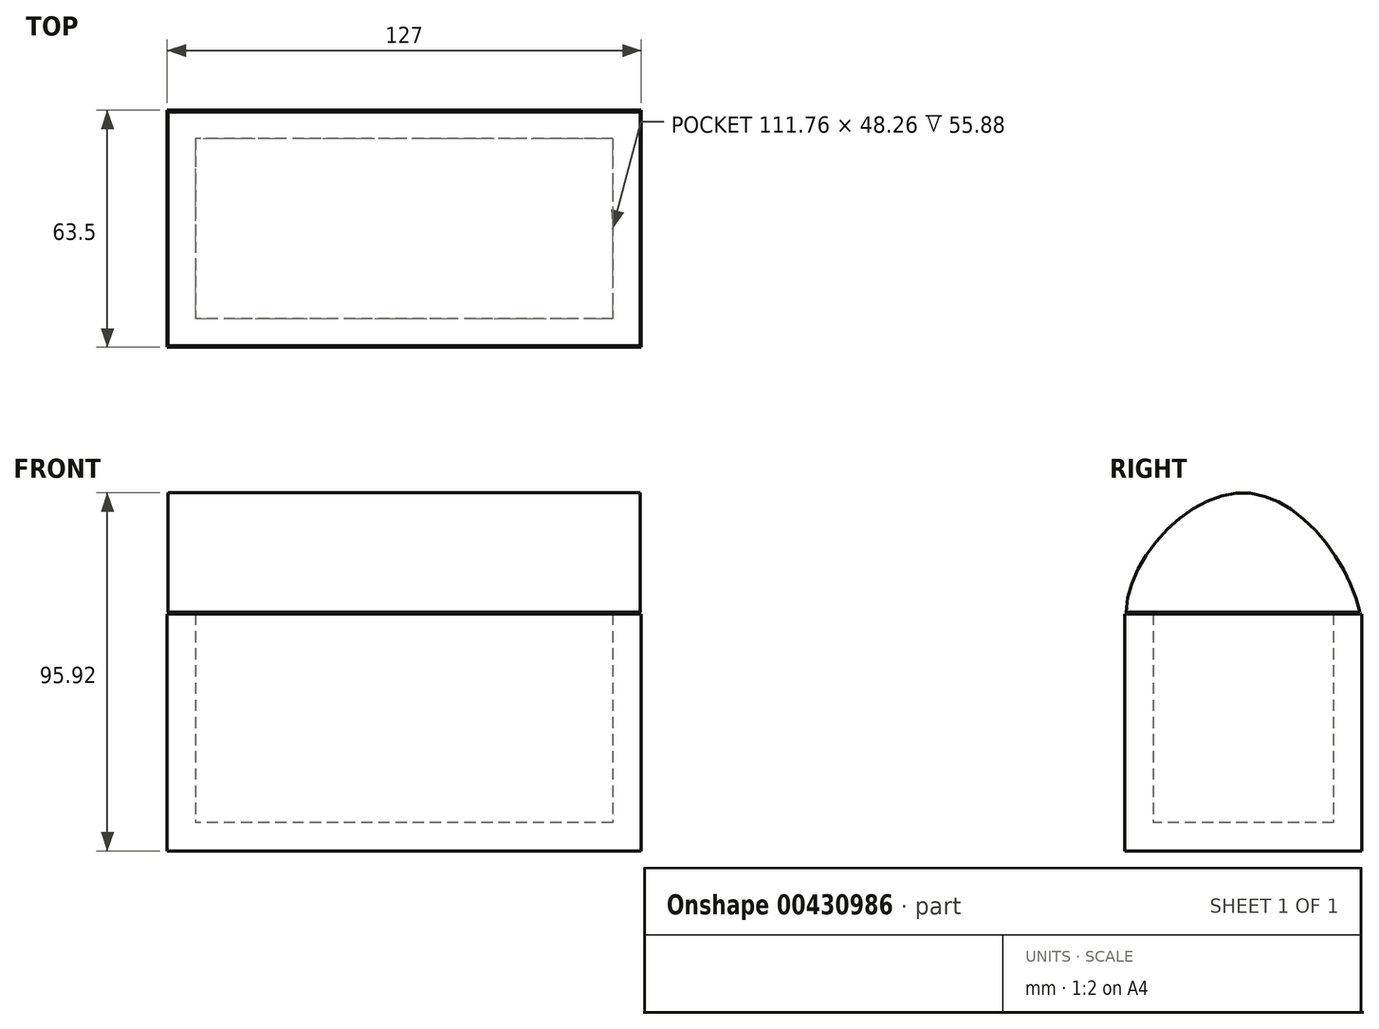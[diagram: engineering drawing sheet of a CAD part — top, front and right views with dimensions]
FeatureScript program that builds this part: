
annotation { "Feature Type Name" : "Feature", "Feature Type Description" : "" }
export const myFeature = defineFeature(function(context is Context, id is Id, definition is map)
    precondition{}
    {
        {
            var Q0;
            Q0=qCreatedBy(makeId("Top.planeOp"),FACE);
            var sketch = newSketch(context, id + "F0", { "sketchPlane" : qUnion([Q0])});
            skLineSegment(sketch, "E0.bottom", {"start": v(63.5, 31.75) * mm, "end": v(-63.5, 31.75) * mm});
            skLineSegment(sketch, "E0.top", {"start": v(63.5, -31.75) * mm, "end": v(-63.5, -31.75) * mm});
            skLineSegment(sketch, "E0.left", {"start": v(63.5, 31.75) * mm, "end": v(63.5, -31.75) * mm});
            skLineSegment(sketch, "E0.right", {"start": v(-63.5, 31.75) * mm, "end": v(-63.5, -31.75) * mm});
            skPoint(sketch, "E0.middle", {"position": v(0, 0) * mm});
            skSolve(sketch);
        }
        {
            var Q0;
            Q0 = qSketchRegion(id + "F0", true);
            extrude(context, id + "F1", {"entities" : qUnion([Q0]), "depth" : 63.5 * mm});
        }
        {
            var Q0;
            Q0=makeQuery(id+"F1.opExtrude","CAP_FACE",FACE,{"disambiguationData":[OSD([sQuery(id+"F0.wireOp",EDGE,"E0.bottom"),sQuery(id+"F0.wireOp",EDGE,"E0.top"),sQuery(id+"F0.wireOp",EDGE,"E0.left"),sQuery(id+"F0.wireOp",EDGE,"E0.right")])],"isStart":false});
            shell(context, id + "F2", {"entities" : qUnion([Q0]), "thickness" : 7.62 * mm});
        }
        {
            var Q0;
            Q0=qCreatedBy(makeId("Right.planeOp"),FACE);
            var sketch = newSketch(context, id + "F3", { "sketchPlane" : qUnion([Q0])});
            skFitSpline(sketch, "E1", {"points": [v(-31.36, 63.95) * mm, v(0, 95.92) * mm, v(31.27, 63.95) * mm], "startDerivative": vector(1.2, 85.9) * mm, "endDerivative": vector(18.93, -83.34) * mm});
            skLineSegment(sketch, "E2", {"start": v(-31.36, 63.95) * mm, "end": v(31.27, 63.95) * mm});
            skSolve(sketch);
        }
        {
            var Q0;
            Q0=makeQuery(id+"F3.imprint","IMPRINT",FACE,{"disambiguationData":[TD([[makeQuery(id+"F3.imprint","IMPRINT",EDGE,{"derivedFrom":sQuery(id+"F3.wireOp",EDGE,"E1")}),-1.0]])]});
            extrude(context, id + "F4", {"entities" : qUnion([Q0]), "depth" : 63.25 * mm, "offsetDistance" : 25.4 * mm, "hasSecondDirection" : true, "secondDirectionOppositeDirection" : true, "secondDirectionDepth" : 63.25 * mm});
        }
    });
